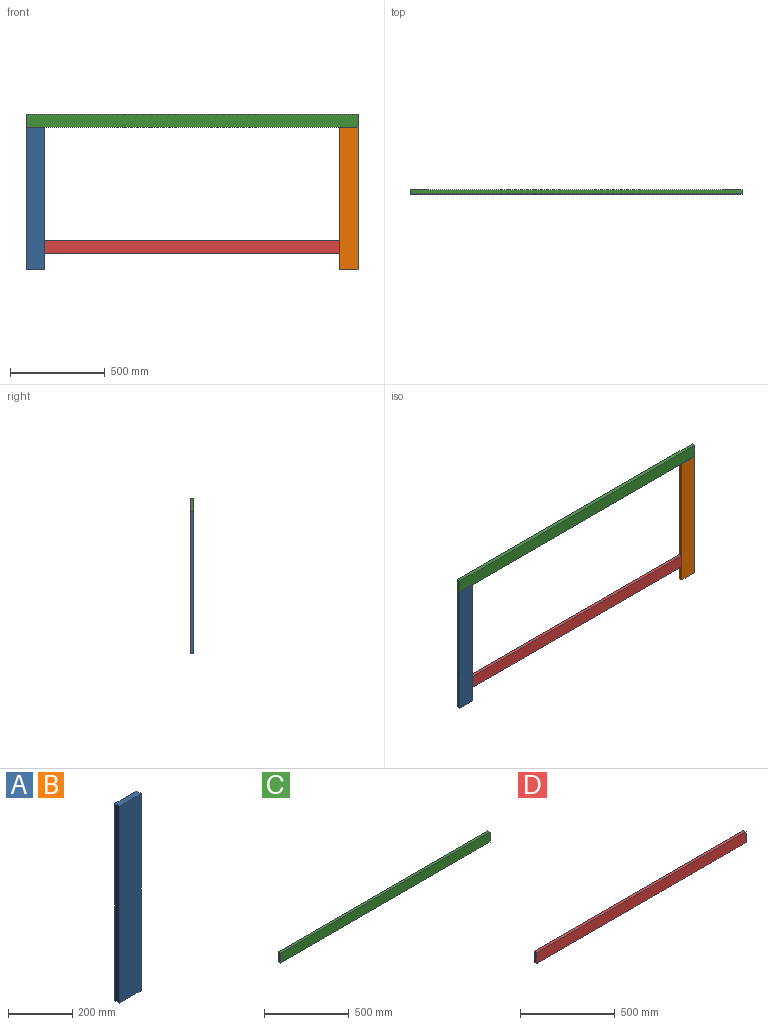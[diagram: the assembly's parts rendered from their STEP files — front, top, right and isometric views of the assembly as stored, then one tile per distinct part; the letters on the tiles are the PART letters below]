
ASSEMBLY  parts=4 mates=3
PART A: 6 faces, bbox 96x20x750 mm
  f0: plane 750x96mm, normal (0,1,0), area 72000mm2, adj f1,f3,f4,f5
  f1: plane 750x20mm, normal (-1,0,0), area 15000mm2, adj f0,f2,f4,f5
  f2: plane 750x96mm, normal (0,-1,0), area 72000mm2, adj f1,f3,f4,f5
  f3: plane 750x20mm, normal (1,0,0), area 15000mm2, adj f0,f2,f4,f5
  f4: plane 96x20mm, normal (0,0,1), area 1920mm2, adj f0,f1,f2,f3
  f5: plane 96x20mm, normal (0,0,-1), area 1920mm2, adj f0,f1,f2,f3
PART B: same geometry as A
PART C: 6 faces, bbox 1750x20x70 mm
  f0: plane 1750x20mm, normal (0,0,-1), area 35000mm2, adj f1,f3,f4,f5
  f1: plane 1750x70mm, normal (0,-1,0), area 122500mm2, adj f0,f2,f4,f5
  f2: plane 1750x20mm, normal (0,0,1), area 35000mm2, adj f1,f3,f4,f5
  f3: plane 1750x70mm, normal (0,1,0), area 122500mm2, adj f0,f2,f4,f5
  f4: plane 70x20mm, normal (1,0,0), area 1400mm2, adj f0,f1,f2,f3
  f5: plane 70x20mm, normal (-1,0,0), area 1400mm2, adj f0,f1,f2,f3
PART D: 6 faces, bbox 1558x20x70 mm
  f0: plane 70x20mm, normal (1,0,0), area 1400mm2, adj f1,f3,f4,f5
  f1: plane 1558x20mm, normal (0,0,-1), area 31160mm2, adj f0,f2,f3,f4
  f2: plane 70x20mm, normal (-1,0,0), area 1400mm2, adj f1,f3,f4,f5
  f3: plane 1558x70mm, normal (0,1,0), area 109060mm2, adj f0,f1,f2,f5
  f4: plane 1558x70mm, normal (0,-1,0), area 109060mm2, adj f0,f1,f2,f5
  f5: plane 1558x20mm, normal (0,0,1), area 31160mm2, adj f0,f2,f3,f4
PLACE A t=(20,720,0)mm
PLACE B t=(1674,720,0)mm
PLACE C t=(20,720,0)mm
PLACE D t=(20,720,0)mm
MATE fastened D.f4 <-> B.f2  axis (0,-1,0) through (1654,-20,85)mm
MATE fastened A.f2 <-> C.f1  axis (0,-1,0) through (0,-20,750)mm
MATE fastened D.f4 <-> A.f2  axis (0,-1,0) through (96,-20,85)mm
